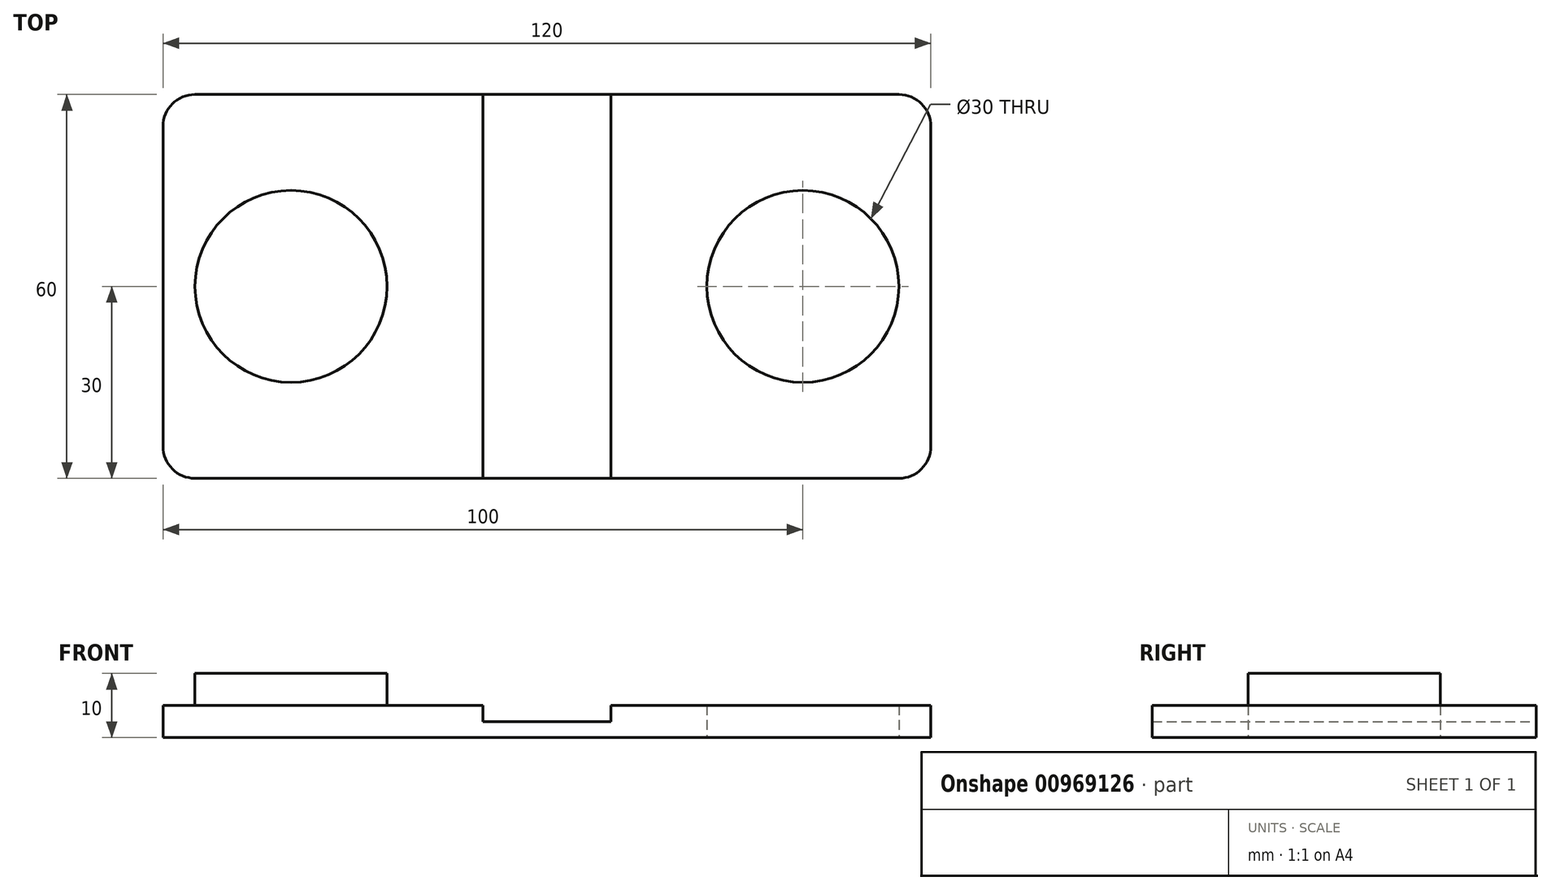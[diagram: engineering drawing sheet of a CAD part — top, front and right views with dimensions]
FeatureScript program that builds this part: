
annotation { "Feature Type Name" : "Feature", "Feature Type Description" : "" }
export const myFeature = defineFeature(function(context is Context, id is Id, definition is map)
    precondition{}
    {
        {
            var Q0;
            Q0=qCreatedBy(makeId("Top.planeOp"),FACE);
            var sketch = newSketch(context, id + "F0", { "sketchPlane" : qUnion([Q0])});
            skLineSegment(sketch, "E0.bottom", {"start": v(60, 30) * mm, "end": v(-60, 30) * mm});
            skLineSegment(sketch, "E0.top", {"start": v(60, -30) * mm, "end": v(-60, -30) * mm});
            skLineSegment(sketch, "E0.left", {"start": v(60, 30) * mm, "end": v(60, -30) * mm});
            skLineSegment(sketch, "E0.right", {"start": v(-60, 30) * mm, "end": v(-60, -30) * mm});
            skPoint(sketch, "E0.middle", {"position": v(0, 0) * mm});
            skCircle(sketch, "E1", {"center": v(40, 0) * mm, "radius": 15 * mm});
            skSolve(sketch);
        }
        {
            var Q0;
            Q0=makeQuery(id+"F0.imprint","IMPRINT",FACE,{"disambiguationData":[TD([[makeQuery(id+"F0.imprint","IMPRINT",EDGE,{"derivedFrom":sQuery(id+"F0.wireOp",EDGE,"E0.bottom")}),1.0]])]});
            extrude(context, id + "F1", {"entities" : qUnion([Q0]), "depth" : 5 * mm, "offsetDistance" : 25 * mm});
        }
        {
            var Q0;
            Q0=makeQuery(id+"F1.opExtrude","SWEPT_EDGE",EDGE,{"disambiguationData":[OSD([sQuery(id+"F0.wireOp",EDGE,"E0.bottom"),sQuery(id+"F0.wireOp",EDGE,"E0.left")])]});
            var Q1;
            Q1=makeQuery(id+"F1.opExtrude","SWEPT_EDGE",EDGE,{"disambiguationData":[OSD([sQuery(id+"F0.wireOp",EDGE,"E0.top"),sQuery(id+"F0.wireOp",EDGE,"E0.left")])]});
            var Q2;
            Q2=makeQuery(id+"F1.opExtrude","SWEPT_EDGE",EDGE,{"disambiguationData":[OSD([sQuery(id+"F0.wireOp",EDGE,"E0.bottom"),sQuery(id+"F0.wireOp",EDGE,"E0.right")])]});
            var Q3;
            Q3=makeQuery(id+"F1.opExtrude","SWEPT_EDGE",EDGE,{"disambiguationData":[OSD([sQuery(id+"F0.wireOp",EDGE,"E0.top"),sQuery(id+"F0.wireOp",EDGE,"E0.right")])]});
            fillet(context, id + "F2", {"entities" : qUnion([Q0, Q1, Q2, Q3]), "radius" : 5 * mm, "tangentPropagation" : true, "allowEdgeOverflow" : false});
        }
        {
            var Q0;
            Q0=makeQuery(id+"F1.opExtrude","CAP_FACE",FACE,{"disambiguationData":[OSD([sQuery(id+"F0.wireOp",EDGE,"E0.bottom"),sQuery(id+"F0.wireOp",EDGE,"E0.top"),sQuery(id+"F0.wireOp",EDGE,"E0.left"),sQuery(id+"F0.wireOp",EDGE,"E0.right"),sQuery(id+"F0.wireOp",EDGE,"E1")])],"isStart":false});
            var sketch = newSketch(context, id + "F3", { "sketchPlane" : qUnion([Q0])});
            skCircle(sketch, "E2", {"center": v(-40, 0) * mm, "radius": 15 * mm});
            skSolve(sketch);
        }
        {
            var Q0;
            Q0 = qSketchRegion(id + "F3", true);
            extrude(context, id + "F4", {"entities" : qUnion([Q0]), "operationType" : NewBodyOperationType.ADD, "depth" : 5 * mm, "offsetDistance" : 25 * mm});
        }
        {
            var Q0;
            Q0=makeQuery(id+"F1.opExtrude","CAP_FACE",FACE,{"disambiguationData":[OSD([sQuery(id+"F0.wireOp",EDGE,"E0.bottom"),sQuery(id+"F0.wireOp",EDGE,"E0.top"),sQuery(id+"F0.wireOp",EDGE,"E0.left"),sQuery(id+"F0.wireOp",EDGE,"E0.right"),sQuery(id+"F0.wireOp",EDGE,"E1")])],"isStart":false});
            var sketch = newSketch(context, id + "F5", { "sketchPlane" : qUnion([Q0])});
            skLineSegment(sketch, "E3", {"start": v(-10, -30) * mm, "end": v(-10, 30) * mm});
            skLineSegment(sketch, "E4", {"start": v(-10, 30) * mm, "end": v(10, 30) * mm});
            skLineSegment(sketch, "E5", {"start": v(10, 30) * mm, "end": v(10, -30) * mm});
            skLineSegment(sketch, "E6", {"start": v(10, -30) * mm, "end": v(-10, -30) * mm});
            skSolve(sketch);
        }
        {
            var Q0;
            Q0=makeQuery(id+"F5.imprint","IMPRINT",FACE,{"disambiguationData":[TD([[makeQuery(id+"F5.imprint","IMPRINT",EDGE,{"derivedFrom":sQuery(id+"F5.wireOp",EDGE,"E3")}),-1.0]])]});
            var Q1;
            Q1=sQuery(id+"F5.wireOp",EDGE,"E4");
            var Q2;
            Q2=sQuery(id+"F5.wireOp",EDGE,"E6");
            var Q3;
            Q3=sQuery(id+"F5.wireOp",EDGE,"E5");
            var Q4;
            Q4=sQuery(id+"F5.wireOp",EDGE,"E3");
            extrude(context, id + "F6", {"entities" : qUnion([Q0]), "operationType" : NewBodyOperationType.REMOVE, "surfaceEntities" : qUnion([Q1, Q2, Q3, Q4]), "oppositeDirection" : true, "depth" : 2.5 * mm, "offsetDistance" : 25 * mm});
        }
    });
